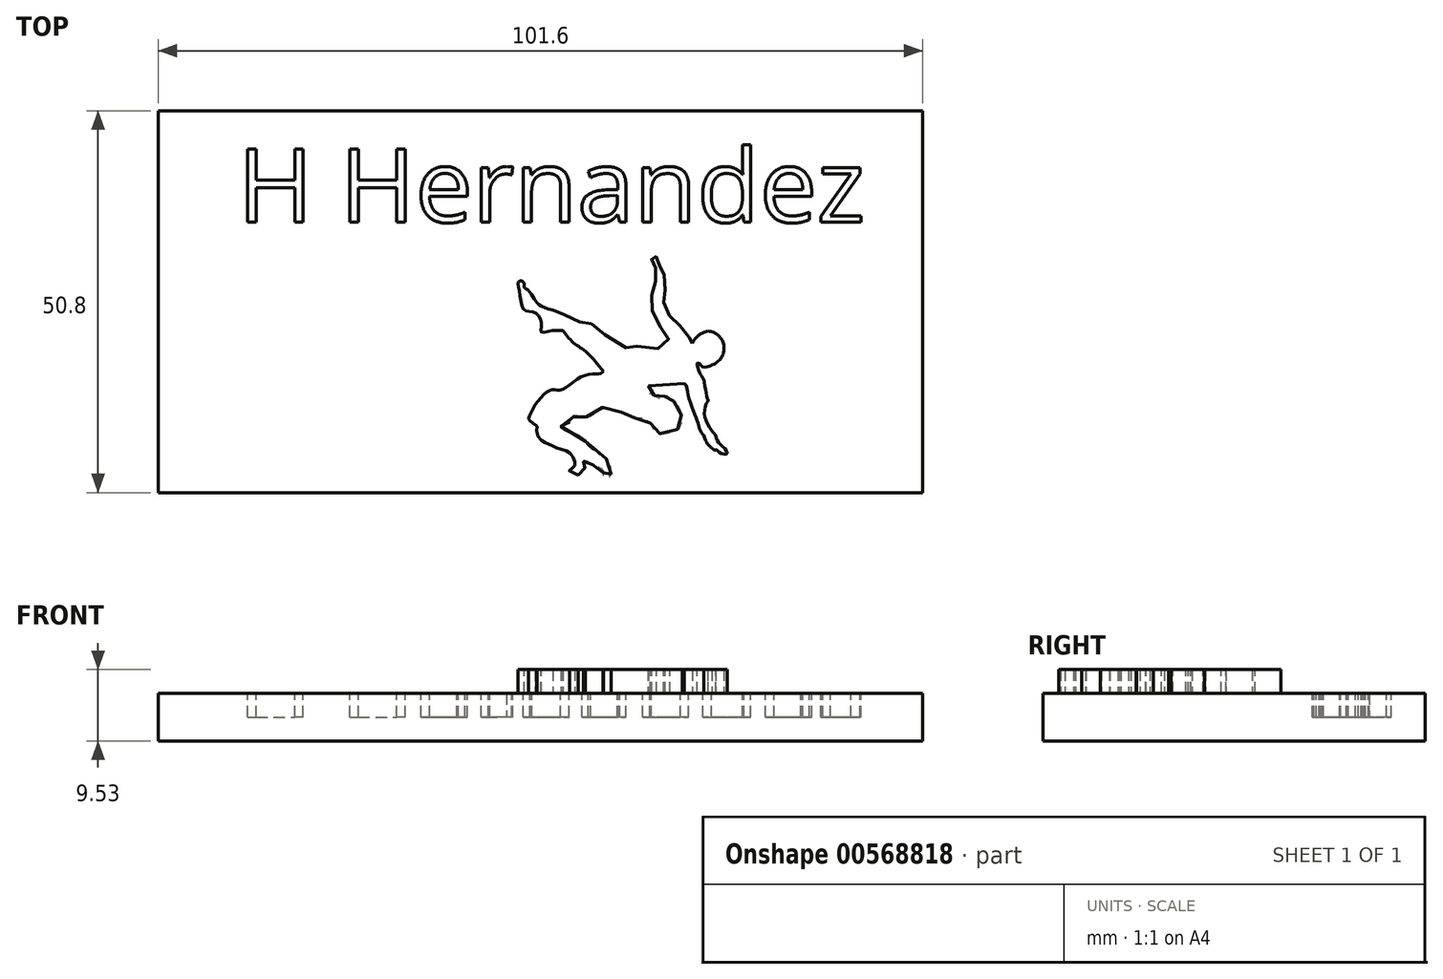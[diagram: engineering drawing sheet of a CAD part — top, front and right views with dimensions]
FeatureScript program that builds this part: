
annotation { "Feature Type Name" : "Feature", "Feature Type Description" : "" }
export const myFeature = defineFeature(function(context is Context, id is Id, definition is map)
    precondition{}
    {
        {
            var Q0;
            Q0=qCreatedBy(makeId("Top.planeOp"),FACE);
            var sketch = newSketch(context, id + "F0", { "sketchPlane" : qUnion([Q0])});
            skLineSegment(sketch, "E0.bottom", {"start": v(-23.9, 0) * mm, "end": v(-125.5, 0) * mm});
            skLineSegment(sketch, "E0.top", {"start": v(-23.9, 50.8) * mm, "end": v(-125.5, 50.8) * mm});
            skLineSegment(sketch, "E0.left", {"start": v(-23.9, 0) * mm, "end": v(-23.9, 50.8) * mm});
            skLineSegment(sketch, "E0.right", {"start": v(-125.5, 0) * mm, "end": v(-125.5, 50.8) * mm});
            skPoint(sketch, "E1.oppositeSnap0", {"position": v(-23.9, 25.4) * mm});
            skLineSegment(sketch, "E1.left", {"start": v(-23.9, 25.4) * mm, "end": v(-23.9, 25.4) * mm});
            skSolve(sketch);
        }
        {
            var Q0;
            Q0 = qSketchRegion(id + "F0", true);
            extrude(context, id + "F1", {"entities" : qUnion([Q0]), "depth" : 6.35 * mm, "offsetDistance" : 25.4 * mm});
        }
        {
            var Q0;
            Q0=makeQuery(id+"F1.opExtrude","CAP_FACE",FACE,{"disambiguationData":[OSD([sQuery(id+"F0.wireOp",EDGE,"E0.bottom"),sQuery(id+"F0.wireOp",EDGE,"E0.top"),sQuery(id+"F0.wireOp",EDGE,"E0.left"),sQuery(id+"F0.wireOp",EDGE,"E0.right")])],"isStart":false});
            var sketch = newSketch(context, id + "F2", { "sketchPlane" : qUnion([Q0])});
            skText(sketch, "E2", { "text": " H Hernandez ", "fontName": "OpenSans-Regular.ttf"});
            const initialGuessF2  = {"E2": [-0.11848, 0.03598, 1, 0, 0.00979]};
            skSetInitialGuess(sketch, initialGuessF2);
            skSolve(sketch);
        }
        {
            var Q0;
            Q0 = qSketchRegion(id + "F2", true);
            extrude(context, id + "F3", {"entities" : qUnion([Q0]), "operationType" : NewBodyOperationType.ADD, "oppositeDirection" : true, "depth" : 3.17 * mm, "offsetDistance" : 25.4 * mm});
        }
        {
            var Q0;
            Q0 = qSketchRegion(id + "F2", true);
            extrude(context, id + "F4", {"entities" : qUnion([Q0]), "operationType" : NewBodyOperationType.REMOVE, "oppositeDirection" : true, "depth" : 3.17 * mm, "offsetDistance" : 25.4 * mm});
        }
        {
            var Q0;
            {var subQ0=sQuery(id+"F0.wireOp",EDGE,"E0.right");var subQ1=sQuery(id+"F0.wireOp",EDGE,"E0.left");var subQ2=sQuery(id+"F0.wireOp",EDGE,"E0.bottom");var subQ3=sQuery(id+"F0.wireOp",EDGE,"E0.top");Q0=makeQuery(id+"F4.boolean.opBoolean","SPLIT",FACE,{"disambiguationData":[TD([makeQuery(id+"F1.opExtrude","SWEPT_FACE",FACE,{"disambiguationData":[OSD([subQ2])]})])],"derivedFrom":makeQuery(id+"F1.opExtrude","CAP_FACE",FACE,{"disambiguationData":[OSD([subQ2,subQ3,subQ1,subQ0])],"isStart":false})});}
            var sketch = newSketch(context, id + "F5", { "sketchPlane" : qUnion([Q0])});
            skSolve(sketch);
        }
        {
            var Q0;
            Q0=makeQuery(id+"F5.imprint","IMPRINT",FACE,{"disambiguationData":[TD([[makeQuery(id+"F5.imprint","IMPRINT",EDGE,{"derivedFrom":makeQuery(id+"F1.opExtrude","CAP_EDGE",EDGE,{"disambiguationData":[OSD([sQuery(id+"F0.wireOp",EDGE,"E0.bottom")])],"isStart":false})}),-1.0]])]});
            var sketch = newSketch(context, id + "F6", { "sketchPlane" : qUnion([Q0])});
            skFitSpline(sketch, "E3", {"points": [v(-75.42, 11.7) * mm, v(-73.3, 13.68) * mm, v(-71.95, 13.68) * mm, v(-68.95, 15.57) * mm, v(-66.9, 15.8) * mm, v(-66.35, 16.13) * mm], "startDerivative": vector(9.11, 11.18) * mm, "endDerivative": vector(3.94, 3.47) * mm});
            skFitSpline(sketch, "E4", {"points": [v(-71.72, 21.57) * mm, v(-70.3, 19.91) * mm, v(-68.72, 18.8) * mm, v(-66.35, 16.13) * mm], "startDerivative": vector(4.38, -5.93) * mm, "endDerivative": vector(6.06, -7.76) * mm});
            skArc(sketch, "E5", {"start": v(-52.46, 21.5) * mm, "mid": v(-53.7, 20.92) * mm, "end": v(-54.51, 19.83) * mm});
            skArc(sketch, "E6", {"start": v(-51.94, 17) * mm, "mid": v(-50.32, 19.46) * mm, "end": v(-52.46, 21.5) * mm});
            skPoint(sketch, "E7.1.internal.orphan", {"position": v(-51.94, 12.57) * mm});
            skPoint(sketch, "E8.0.internal.orphan", {"position": v(-55.85, 14.53) * mm});
            skPoint(sketch, "E9.end.orphan", {"position": v(-55.85, 15.14) * mm});
            skLineSegment(sketch, "E10", {"start": v(-60.35, 14.22) * mm, "end": v(-55.6, 14.53) * mm});
            skFitSpline(sketch, "E11", {"points": [v(-55.6, 14.53) * mm, v(-55.33, 14.25) * mm, v(-55.08, 12.9) * mm, v(-53.9, 9.7) * mm, v(-53.62, 8.78) * mm, v(-53.21, 7.86) * mm, v(-52.9, 7.56) * mm, v(-52.97, 7.52) * mm, v(-52.99, 7.52) * mm], "startDerivative": vector(3.4, -2.35) * mm, "endDerivative": vector(-0.71, 0.14) * mm});
            skPoint(sketch, "E12.endDerivative.orphan", {"position": v(-52.78, 14.53) * mm});
            skPoint(sketch, "E13.1.internal.orphan", {"position": v(-53.88, 17) * mm});
            skPoint(sketch, "E14.6.internal.orphan", {"position": v(-53.36, 17) * mm});
            skFitSpline(sketch, "E15", {"points": [v(-51.94, 17) * mm, v(-52.33, 16.8) * mm, v(-53.18, 16.76) * mm, v(-53.43, 17.04) * mm, v(-53.55, 17.2) * mm, v(-53.87, 17.23) * mm, v(-53.88, 17) * mm, v(-53.74, 16.49) * mm, v(-53.36, 15.63) * mm, v(-53.08, 15.2) * mm, v(-52.96, 14.9) * mm, v(-52.92, 14.7) * mm], "startDerivative": vector(-3.49, -2.16) * mm, "endDerivative": vector(0.3, -3.13) * mm});
            skFitSpline(sketch, "E16", {"points": [v(-52.92, 14.7) * mm, v(-52.49, 12.4) * mm, v(-52.46, 12.4) * mm, v(-52.4, 12.42) * mm, v(-52.92, 10.63) * mm, v(-51.5, 7.73) * mm, v(-51.4, 7.62) * mm, v(-51.4, 7.68) * mm], "startDerivative": vector(2.06, -12.45) * mm, "endDerivative": vector(-0.2, 1.78) * mm});
            skFitSpline(sketch, "E17", {"points": [v(-75.42, 11.7) * mm, v(-76.28, 9.94) * mm, v(-76.24, 9.75) * mm, v(-75.81, 9.3) * mm, v(-75.2, 8.86) * mm, v(-75.18, 8.86) * mm, v(-75.13, 7.75) * mm, v(-74.12, 6.65) * mm, v(-73.46, 6.37) * mm, v(-72.1, 5.8) * mm, v(-70.87, 5.36) * mm, v(-70.14, 4.1) * mm, v(-70.3, 3.42) * mm, v(-70.84, 2.97) * mm, v(-70.85, 2.9) * mm, v(-70.82, 2.94) * mm], "startDerivative": vector(-10.6, -19.88) * mm, "endDerivative": vector(2.28, 3.01) * mm});
            skFitSpline(sketch, "E18", {"points": [v(-69.7, 2.33) * mm, v(-69.18, 2.8) * mm, v(-69.18, 2.94) * mm, v(-68.77, 3.33) * mm, v(-68.76, 3.42) * mm, v(-68.8, 4.1) * mm, v(-68.95, 4.07) * mm, v(-68.92, 4.28) * mm, v(-68.58, 4.27) * mm, v(-67.98, 3.79) * mm, v(-67.25, 3.64) * mm, v(-66.33, 2.77) * mm, v(-66.33, 2.25) * mm, v(-65.49, 2.2) * mm, v(-65.44, 3.54) * mm, v(-65.92, 4.5) * mm, v(-66.88, 5.22) * mm, v(-67.27, 5.63) * mm, v(-68.1, 6.17) * mm, v(-68.8, 6.89) * mm, v(-70.14, 7.8) * mm, v(-71.2, 8.26) * mm, v(-71.76, 8.55) * mm, v(-71.95, 8.82) * mm, v(-70.77, 9.45) * mm, v(-70.14, 10.35) * mm, v(-69.78, 10.28) * mm, v(-68.02, 10.22) * mm, v(-66.53, 11.35) * mm, v(-65.13, 11.01) * mm, v(-63.2, 10.42) * mm, v(-62.68, 10.02) * mm, v(-60.75, 9.92) * mm, v(-60.06, 9.16) * mm, v(-59.66, 8.43) * mm, v(-58.3, 7.73) * mm, v(-56.6, 8.4) * mm, v(-55.94, 8.99) * mm, v(-56.04, 10.78) * mm, v(-56.67, 12.04) * mm, v(-57.43, 12.37) * mm, v(-57.77, 12.84) * mm, v(-58.33, 12.74) * mm, v(-58.93, 12.44) * mm, v(-59.6, 12.94) * mm, v(-60.35, 13.34) * mm, v(-60.35, 14.22) * mm], "startDerivative": vector(38.86, 27.65) * mm, "endDerivative": vector(9.78, 47.6) * mm});
            skPoint(sketch, "E19.1.internal.orphan", {"position": v(-77.71, 27.81) * mm});
            skPoint(sketch, "E19.2.internal.orphan", {"position": v(-76.87, 24.33) * mm});
            skPoint(sketch, "E19.3.internal.orphan", {"position": v(-75.27, 24.33) * mm});
            skPoint(sketch, "E20.start.orphan", {"position": v(-76.87, 27.81) * mm});
            skFitSpline(sketch, "E21", {"points": [v(-71.72, 21.57) * mm, v(-72.35, 21.57) * mm, v(-73.05, 21.57) * mm, v(-74.58, 21.34) * mm, v(-74.6, 21.97) * mm, v(-74.8, 23.36) * mm, v(-75.84, 24.1) * mm, v(-76.87, 24.33) * mm, v(-77.42, 26.23) * mm, v(-77.71, 27.81) * mm], "startDerivative": vector(-8.06, -0.26) * mm, "endDerivative": vector(-2.35, 10.91) * mm});
            skFitSpline(sketch, "E22", {"points": [v(-77.71, 27.81) * mm, v(-77.42, 28.19) * mm, v(-76.87, 27.81) * mm, v(-76.87, 27.34) * mm, v(-76.46, 27.03) * mm, v(-75.63, 25.93) * mm, v(-74.8, 24.94) * mm, v(-73.22, 24.33) * mm, v(-73.05, 24.33) * mm], "startDerivative": vector(2.18, 5.34) * mm, "endDerivative": vector(1.95, 0.34) * mm});
            skPoint(sketch, "E23.3.internal.orphan", {"position": v(-63.2, 19.28) * mm});
            skPoint(sketch, "E23.5.internal.orphan", {"position": v(-60.75, 19.04) * mm});
            skPoint(sketch, "E23.6.internal.orphan", {"position": v(-57.43, 19.68) * mm});
            skFitSpline(sketch, "E24", {"points": [v(-73.05, 24.33) * mm, v(-71.66, 23.68) * mm, v(-71.6, 23.68) * mm, v(-69.58, 22.83) * mm, v(-69.34, 22.62) * mm, v(-68, 22.5) * mm, v(-66.62, 21.43) * mm, v(-63.2, 19.28) * mm, v(-62.35, 19.67) * mm, v(-60.75, 19.04) * mm, v(-57.5, 20.04) * mm, v(-58.08, 20.84) * mm, v(-58.76, 22.1) * mm, v(-59.91, 24.33) * mm, v(-60, 25.95) * mm, v(-59.51, 27.9) * mm, v(-59.4, 28.2) * mm, v(-59.35, 29.73) * mm, v(-59.81, 30.64) * mm, v(-59.88, 30.83) * mm, v(-59.88, 31.54) * mm, v(-59.4, 31.56) * mm, v(-59.34, 31.33) * mm, v(-58.97, 30.81) * mm, v(-58.87, 30.12) * mm, v(-58.4, 29.37) * mm, v(-58.24, 28.23) * mm, v(-58.18, 26.65) * mm, v(-58.34, 25.72) * mm, v(-57.98, 24) * mm, v(-57.07, 23.18) * mm, v(-55.95, 22) * mm, v(-55, 20.81) * mm, v(-54.79, 19.61) * mm, v(-54.51, 19.83) * mm], "startDerivative": vector(55.75, -28.07) * mm, "endDerivative": vector(19.55, 23.87) * mm});
            skFitSpline(sketch, "E25", {"points": [v(-52.98, 7.52) * mm, v(-52.66, 6.77) * mm, v(-52.43, 6.44) * mm, v(-51.5, 5.66) * mm, v(-51.33, 5.71) * mm, v(-50.83, 5.31) * mm, v(-49.92, 5.2) * mm, v(-50.2, 5.87) * mm, v(-51.1, 6.74) * mm, v(-51.4, 7.65) * mm], "startDerivative": vector(3.03, -7.47) * mm, "endDerivative": vector(-1.37, 7.63) * mm});
            skFitSpline(sketch, "E26", {"points": [v(-70.82, 2.94) * mm, v(-69.7, 2.33) * mm], "startDerivative": vector(1.11, -0.6) * mm, "endDerivative": vector(1.11, -0.6) * mm});
            skLineSegment(sketch, "E27", {"start": v(-51.4, 7.62) * mm, "end": v(-51.39, 7.6) * mm});
            skSolve(sketch);
        }
        {
            var Q0;
            Q0 = qSketchRegion(id + "F6", true);
            extrude(context, id + "F7", {"entities" : qUnion([Q0]), "operationType" : NewBodyOperationType.ADD, "depth" : 3.17 * mm, "offsetDistance" : 25.4 * mm});
        }
    });
